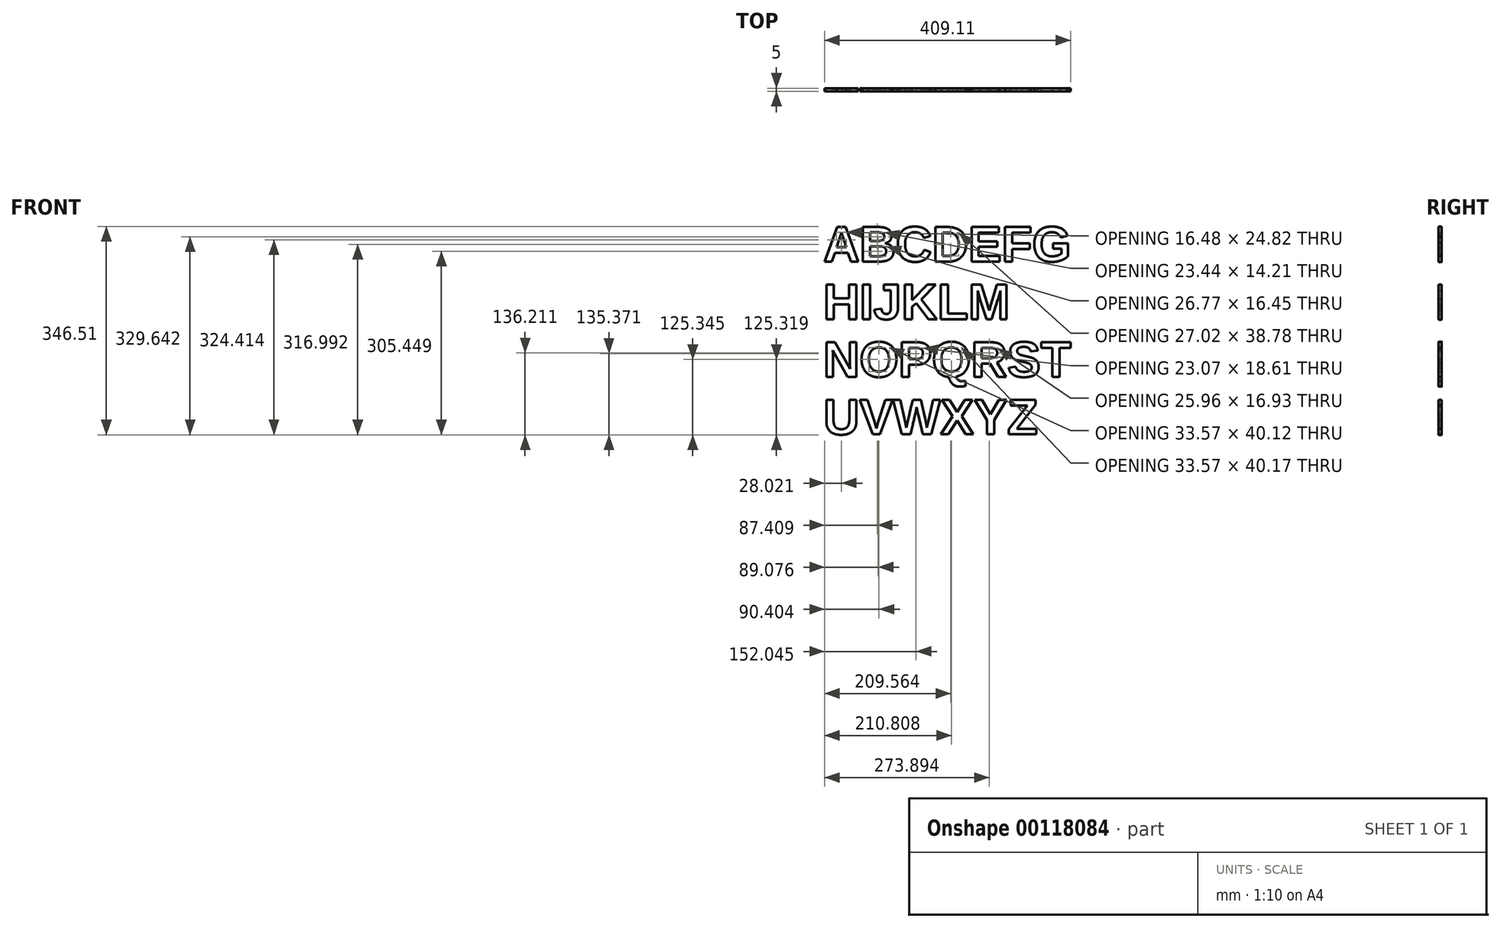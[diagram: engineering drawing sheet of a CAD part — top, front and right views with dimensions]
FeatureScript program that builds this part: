
annotation { "Feature Type Name" : "Feature", "Feature Type Description" : "" }
export const myFeature = defineFeature(function(context is Context, id is Id, definition is map)
    precondition{}
    {
        {
            var Q0;
            Q0=qCreatedBy(makeId("Front.planeOp"),FACE);
            var sketch = newSketch(context, id + "F0", { "sketchPlane" : qUnion([Q0])});
            skText(sketch, "E0", { "text": "ABCDEFG\nHIJKLM\nNOPQRST\nUVWXYZ", "fontName": "Arimo-Bold.ttf"});
            const initialGuessF0  = {"E0": [0, 0, 1, 0, 0.06]};
            skSetInitialGuess(sketch, initialGuessF0);
            skSolve(sketch);
        }
        {
            var Q0;
            Q0=makeQuery(id+"F0.imprint","IMPRINT",FACE,{"disambiguationData":[TD([[makeQuery(id+"F0.imprint","IMPRINT",EDGE,{"derivedFrom":sQuery(id+"F0.wireOp",EDGE,"E0.sketch_text.stroke-0")}),-1.0]])]});
            var Q1;
            Q1=makeQuery(id+"F0.imprint","IMPRINT",FACE,{"disambiguationData":[TD([[makeQuery(id+"F0.imprint","IMPRINT",EDGE,{"derivedFrom":sQuery(id+"F0.wireOp",EDGE,"E0.sketch_text.stroke-15")}),-1.0]])]});
            var Q2;
            Q2=makeQuery(id+"F0.imprint","IMPRINT",FACE,{"disambiguationData":[TD([[makeQuery(id+"F0.imprint","IMPRINT",EDGE,{"derivedFrom":sQuery(id+"F0.wireOp",EDGE,"E0.sketch_text.stroke-39")}),-1.0]])]});
            var Q3;
            Q3=makeQuery(id+"F0.imprint","IMPRINT",FACE,{"disambiguationData":[TD([[makeQuery(id+"F0.imprint","IMPRINT",EDGE,{"derivedFrom":sQuery(id+"F0.wireOp",EDGE,"E0.sketch_text.stroke-56")}),-1.0]])]});
            var Q4;
            Q4=makeQuery(id+"F0.imprint","IMPRINT",FACE,{"disambiguationData":[TD([[makeQuery(id+"F0.imprint","IMPRINT",EDGE,{"derivedFrom":sQuery(id+"F0.wireOp",EDGE,"E0.sketch_text.stroke-71")}),-1.0]])]});
            var Q5;
            Q5=makeQuery(id+"F0.imprint","IMPRINT",FACE,{"disambiguationData":[TD([[makeQuery(id+"F0.imprint","IMPRINT",EDGE,{"derivedFrom":sQuery(id+"F0.wireOp",EDGE,"E0.sketch_text.stroke-83")}),-1.0]])]});
            var Q6;
            Q6=makeQuery(id+"F0.imprint","IMPRINT",FACE,{"disambiguationData":[TD([[makeQuery(id+"F0.imprint","IMPRINT",EDGE,{"derivedFrom":sQuery(id+"F0.wireOp",EDGE,"E0.sketch_text.stroke-93")}),-1.0]])]});
            var Q7;
            Q7=makeQuery(id+"F0.imprint","IMPRINT",FACE,{"disambiguationData":[TD([[makeQuery(id+"F0.imprint","IMPRINT",EDGE,{"derivedFrom":sQuery(id+"F0.wireOp",EDGE,"E0.sketch_text.stroke-114")}),-1.0]])]});
            var Q8;
            Q8=makeQuery(id+"F0.imprint","IMPRINT",FACE,{"disambiguationData":[TD([[makeQuery(id+"F0.imprint","IMPRINT",EDGE,{"derivedFrom":sQuery(id+"F0.wireOp",EDGE,"E0.sketch_text.stroke-126")}),-1.0]])]});
            var Q9;
            Q9=makeQuery(id+"F0.imprint","IMPRINT",FACE,{"disambiguationData":[TD([[makeQuery(id+"F0.imprint","IMPRINT",EDGE,{"derivedFrom":sQuery(id+"F0.wireOp",EDGE,"E0.sketch_text.stroke-130")}),-1.0]])]});
            var Q10;
            Q10=makeQuery(id+"F0.imprint","IMPRINT",FACE,{"disambiguationData":[TD([[makeQuery(id+"F0.imprint","IMPRINT",EDGE,{"derivedFrom":sQuery(id+"F0.wireOp",EDGE,"E0.sketch_text.stroke-144")}),-1.0]])]});
            var Q11;
            Q11=makeQuery(id+"F0.imprint","IMPRINT",FACE,{"disambiguationData":[TD([[makeQuery(id+"F0.imprint","IMPRINT",EDGE,{"derivedFrom":sQuery(id+"F0.wireOp",EDGE,"E0.sketch_text.stroke-156")}),-1.0]])]});
            var Q12;
            Q12=makeQuery(id+"F0.imprint","IMPRINT",FACE,{"disambiguationData":[TD([[makeQuery(id+"F0.imprint","IMPRINT",EDGE,{"derivedFrom":sQuery(id+"F0.wireOp",EDGE,"E0.sketch_text.stroke-162")}),-1.0]])]});
            var Q13;
            Q13=makeQuery(id+"F0.imprint","IMPRINT",FACE,{"disambiguationData":[TD([[makeQuery(id+"F0.imprint","IMPRINT",EDGE,{"derivedFrom":sQuery(id+"F0.wireOp",EDGE,"E0.sketch_text.stroke-183")}),-1.0]])]});
            var Q14;
            Q14=makeQuery(id+"F0.imprint","IMPRINT",FACE,{"disambiguationData":[TD([[makeQuery(id+"F0.imprint","IMPRINT",EDGE,{"derivedFrom":sQuery(id+"F0.wireOp",EDGE,"E0.sketch_text.stroke-195")}),-1.0]])]});
            var Q15;
            Q15=makeQuery(id+"F0.imprint","IMPRINT",FACE,{"disambiguationData":[TD([[makeQuery(id+"F0.imprint","IMPRINT",EDGE,{"derivedFrom":sQuery(id+"F0.wireOp",EDGE,"E0.sketch_text.stroke-212")}),-1.0]])]});
            var Q16;
            Q16=makeQuery(id+"F0.imprint","IMPRINT",FACE,{"disambiguationData":[TD([[makeQuery(id+"F0.imprint","IMPRINT",EDGE,{"derivedFrom":sQuery(id+"F0.wireOp",EDGE,"E0.sketch_text.stroke-228")}),-1.0]])]});
            var Q17;
            Q17=makeQuery(id+"F0.imprint","IMPRINT",FACE,{"disambiguationData":[TD([[makeQuery(id+"F0.imprint","IMPRINT",EDGE,{"derivedFrom":sQuery(id+"F0.wireOp",EDGE,"E0.sketch_text.stroke-251")}),-1.0]])]});
            var Q18;
            Q18=makeQuery(id+"F0.imprint","IMPRINT",FACE,{"disambiguationData":[TD([[makeQuery(id+"F0.imprint","IMPRINT",EDGE,{"derivedFrom":sQuery(id+"F0.wireOp",EDGE,"E0.sketch_text.stroke-269")}),-1.0]])]});
            var Q19;
            Q19=makeQuery(id+"F0.imprint","IMPRINT",FACE,{"disambiguationData":[TD([[makeQuery(id+"F0.imprint","IMPRINT",EDGE,{"derivedFrom":sQuery(id+"F0.wireOp",EDGE,"E0.sketch_text.stroke-300")}),-1.0]])]});
            var Q20;
            Q20=makeQuery(id+"F0.imprint","IMPRINT",FACE,{"disambiguationData":[TD([[makeQuery(id+"F0.imprint","IMPRINT",EDGE,{"derivedFrom":sQuery(id+"F0.wireOp",EDGE,"E0.sketch_text.stroke-308")}),-1.0]])]});
            var Q21;
            Q21=makeQuery(id+"F0.imprint","IMPRINT",FACE,{"disambiguationData":[TD([[makeQuery(id+"F0.imprint","IMPRINT",EDGE,{"derivedFrom":sQuery(id+"F0.wireOp",EDGE,"E0.sketch_text.stroke-322")}),-1.0]])]});
            var Q22;
            Q22=makeQuery(id+"F0.imprint","IMPRINT",FACE,{"disambiguationData":[TD([[makeQuery(id+"F0.imprint","IMPRINT",EDGE,{"derivedFrom":sQuery(id+"F0.wireOp",EDGE,"E0.sketch_text.stroke-332")}),-1.0]])]});
            var Q23;
            Q23=makeQuery(id+"F0.imprint","IMPRINT",FACE,{"disambiguationData":[TD([[makeQuery(id+"F0.imprint","IMPRINT",EDGE,{"derivedFrom":sQuery(id+"F0.wireOp",EDGE,"E0.sketch_text.stroke-352")}),-1.0]])]});
            var Q24;
            Q24=makeQuery(id+"F0.imprint","IMPRINT",FACE,{"disambiguationData":[TD([[makeQuery(id+"F0.imprint","IMPRINT",EDGE,{"derivedFrom":sQuery(id+"F0.wireOp",EDGE,"E0.sketch_text.stroke-364")}),-1.0]])]});
            var Q25;
            Q25=makeQuery(id+"F0.imprint","IMPRINT",FACE,{"disambiguationData":[TD([[makeQuery(id+"F0.imprint","IMPRINT",EDGE,{"derivedFrom":sQuery(id+"F0.wireOp",EDGE,"E0.sketch_text.stroke-373")}),-1.0]])]});
            extrude(context, id + "F1", {"entities" : qUnion([Q0, Q1, Q2, Q3, Q4, Q5, Q6, Q7, Q8, Q9, Q10, Q11, Q12, Q13, Q14, Q15, Q16, Q17, Q18, Q19, Q20, Q21, Q22, Q23, Q24, Q25]), "depth" : 5 * mm});
        }
    });
